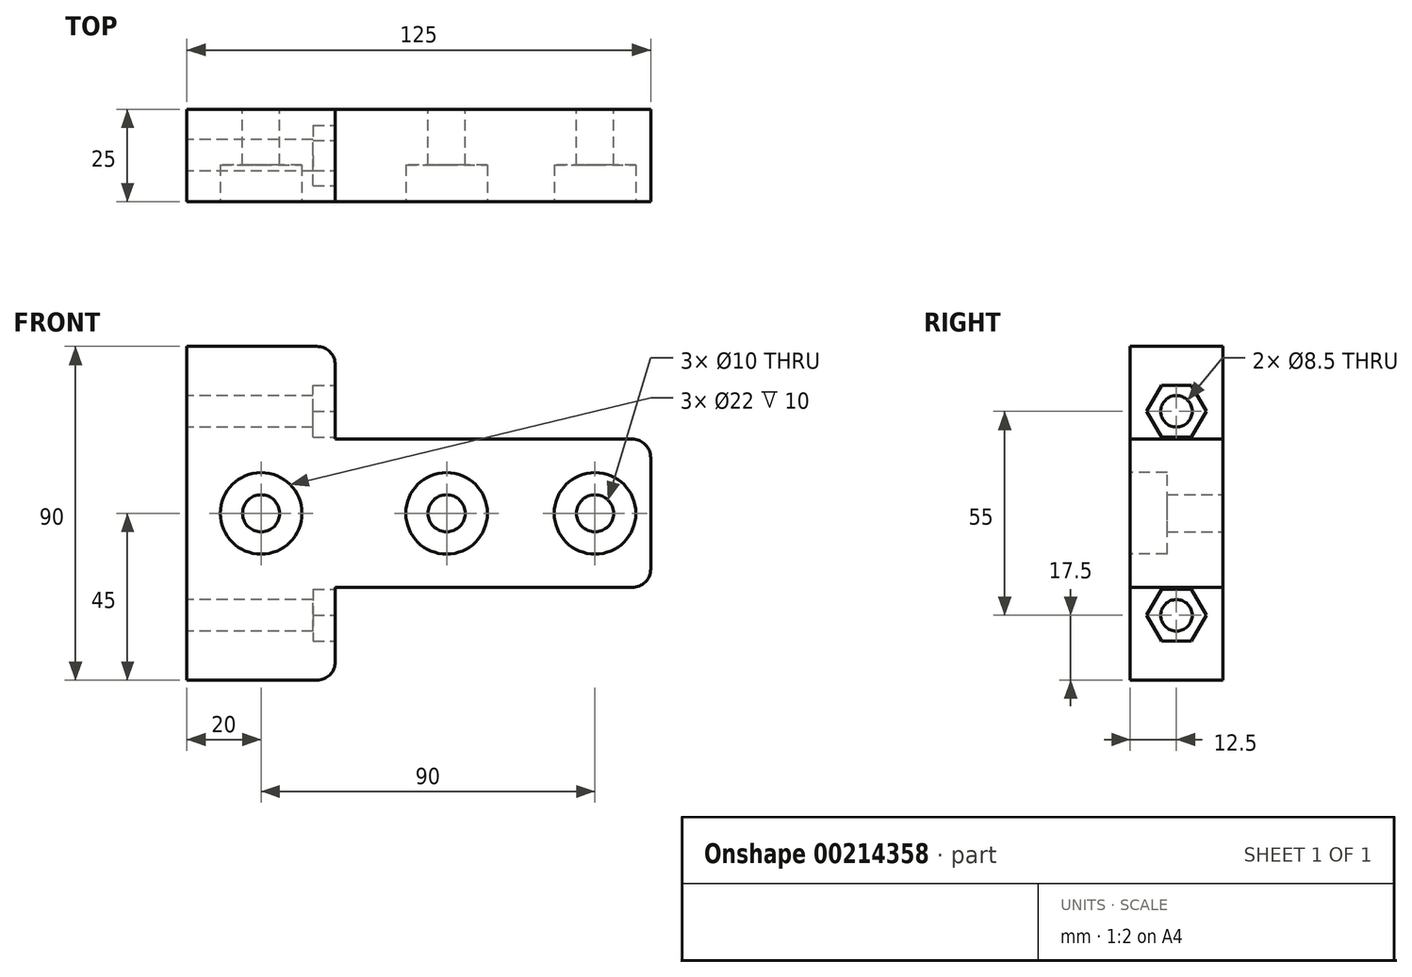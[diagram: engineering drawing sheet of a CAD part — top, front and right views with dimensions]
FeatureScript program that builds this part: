
annotation { "Feature Type Name" : "Feature", "Feature Type Description" : "" }
export const myFeature = defineFeature(function(context is Context, id is Id, definition is map)
    precondition{}
    {
        {
            var Q0;
            Q0=qCreatedBy(makeId("Front.planeOp"),FACE);
            var sketch = newSketch(context, id + "F0", { "sketchPlane" : qUnion([Q0])});
            skLineSegment(sketch, "E0.bottom", {"start": v(55, 20) * mm, "end": v(-70, 20) * mm});
            skLineSegment(sketch, "E0.top", {"start": v(55, -20) * mm, "end": v(-70, -20) * mm});
            skLineSegment(sketch, "E0.right", {"start": v(-70, 20) * mm, "end": v(-70, -20) * mm});
            skPoint(sketch, "E0.middle", {"position": v(0, 0) * mm});
            skCircle(sketch, "E1", {"center": v(0, 0) * mm, "radius": 5 * mm});
            skCircle(sketch, "E2", {"center": v(40, 0) * mm, "radius": 5 * mm});
            skCircle(sketch, "E3", {"center": v(-50, 0) * mm, "radius": 5 * mm});
            skLineSegment(sketch, "E4", {"start": v(55, 20) * mm, "end": v(55, -20) * mm});
            skSolve(sketch);
        }
        {
            var Q0;
            Q0=qSketchRegion(id+"F0",true);
            extrude(context, id + "F1", {"entities" : qUnion([Q0]), "depth" : 25 * mm});
        }
        {
            var Q0;
            Q0=makeQuery(id+"F1.opExtrude","CAP_FACE",FACE,{"disambiguationData":[OSD([sQuery(id+"F0.wireOp",EDGE,"E0.bottom"),sQuery(id+"F0.wireOp",EDGE,"E0.top"),sQuery(id+"F0.wireOp",EDGE,"E0.right"),sQuery(id+"F0.wireOp",EDGE,"E1"),sQuery(id+"F0.wireOp",EDGE,"E2"),sQuery(id+"F0.wireOp",EDGE,"E3"),sQuery(id+"F0.wireOp",EDGE,"E4")])],"isStart":false});
            var sketch = newSketch(context, id + "F2", { "sketchPlane" : qUnion([Q0])});
            skCircle(sketch, "E5", {"center": v(-50, 0) * mm, "radius": 11 * mm});
            skCircle(sketch, "E6", {"center": v(0, 0) * mm, "radius": 11 * mm});
            skCircle(sketch, "E7", {"center": v(40, 0) * mm, "radius": 11 * mm});
            skSolve(sketch);
        }
        {
            var Q0;
            Q0=qSketchRegion(id+"F2",true);
            extrude(context, id + "F3", {"entities" : qUnion([Q0]), "operationType" : NewBodyOperationType.REMOVE, "oppositeDirection" : true, "depth" : 10 * mm});
        }
        {
            var Q0;
            Q0=makeQuery(id+"F1.opExtrude","CAP_FACE",FACE,{"disambiguationData":[OSD([sQuery(id+"F0.wireOp",EDGE,"E0.bottom"),sQuery(id+"F0.wireOp",EDGE,"E0.top"),sQuery(id+"F0.wireOp",EDGE,"E0.right"),sQuery(id+"F0.wireOp",EDGE,"E1"),sQuery(id+"F0.wireOp",EDGE,"E2"),sQuery(id+"F0.wireOp",EDGE,"E3"),sQuery(id+"F0.wireOp",EDGE,"E4")])],"isStart":true});
            var sketch = newSketch(context, id + "F4", { "sketchPlane" : qUnion([Q0])});
            skLineSegment(sketch, "E8", {"start": v(30, 20) * mm, "end": v(30, 45) * mm});
            skLineSegment(sketch, "E9", {"start": v(30, 45) * mm, "end": v(70, 45) * mm});
            skLineSegment(sketch, "E10", {"start": v(70, 45) * mm, "end": v(70, 20) * mm});
            skLineSegment(sketch, "E11", {"start": v(70, 20) * mm, "end": v(30, 20) * mm});
            skLineSegment(sketch, "E12", {"start": v(70, -20) * mm, "end": v(70, -45) * mm});
            skLineSegment(sketch, "E13", {"start": v(70, -45) * mm, "end": v(30, -45) * mm});
            skLineSegment(sketch, "E14", {"start": v(30, -45) * mm, "end": v(30, -20) * mm});
            skLineSegment(sketch, "E15", {"start": v(30, -20) * mm, "end": v(70, -20) * mm});
            skSolve(sketch);
        }
        {
            var Q0;
            Q0=qSketchRegion(id+"F4",true);
            extrude(context, id + "F5", {"entities" : qUnion([Q0]), "operationType" : NewBodyOperationType.ADD, "oppositeDirection" : true, "depth" : 25 * mm});
        }
        {
            var Q0;
            Q0=makeQuery(id+"F5.boolean.opBoolean","MERGE",FACE,{"derivedFrom":[makeQuery(id+"F1.opExtrude","SWEPT_FACE",FACE,{"disambiguationData":[OSD([sQuery(id+"F0.wireOp",EDGE,"E0.right")])]}),makeQuery(id+"F5.opExtrude","SWEPT_FACE",FACE,{"disambiguationData":[OSD([sQuery(id+"F4.wireOp",EDGE,"E10")])]}),makeQuery(id+"F5.opExtrude","SWEPT_FACE",FACE,{"disambiguationData":[OSD([sQuery(id+"F4.wireOp",EDGE,"E12")])]})]});
            var sketch = newSketch(context, id + "F6", { "sketchPlane" : qUnion([Q0])});
            skCircle(sketch, "E16", {"center": v(12.5, 27.5) * mm, "radius": 4.25 * mm});
            skCircle(sketch, "E17", {"center": v(12.5, -27.5) * mm, "radius": 4.25 * mm});
            skSolve(sketch);
        }
        {
            var Q0;
            Q0=qSketchRegion(id+"F6",true);
            extrude(context, id + "F7", {"entities" : qUnion([Q0]), "operationType" : NewBodyOperationType.REMOVE, "endBound" : BoundingType.UP_TO_NEXT, "oppositeDirection" : true, "depth" : 25 * mm});
        }
        {
            var Q0;
            Q0=makeQuery(id+"F5.opExtrude","SWEPT_FACE",FACE,{"disambiguationData":[OSD([sQuery(id+"F4.wireOp",EDGE,"E8")])]});
            var sketch = newSketch(context, id + "F8", { "sketchPlane" : qUnion([Q0])});
            skCircle(sketch, "E18.cCircle", {"center": v(-12.5, 27.5) * mm, "radius": 7 * mm, "construction": true});
            skLineSegment(sketch, "E18.0", {"start": v(-16.54, 34.5) * mm, "end": v(-8.46, 34.5) * mm});
            skLineSegment(sketch, "E18.1", {"start": v(-8.46, 34.5) * mm, "end": v(-4.42, 27.5) * mm});
            skLineSegment(sketch, "E18.2", {"start": v(-4.42, 27.5) * mm, "end": v(-8.46, 20.5) * mm});
            skLineSegment(sketch, "E18.3", {"start": v(-8.46, 20.5) * mm, "end": v(-16.54, 20.5) * mm});
            skLineSegment(sketch, "E18.4", {"start": v(-16.54, 20.5) * mm, "end": v(-20.58, 27.5) * mm});
            skLineSegment(sketch, "E18.5", {"start": v(-20.58, 27.5) * mm, "end": v(-16.54, 34.5) * mm});
            skPoint(sketch, "E18.0.midPoint", {"position": v(-12.5, 34.5) * mm});
            skLineSegment(sketch, "E19.MirrorCS", {"start": v(-16.54, -20.5) * mm, "end": v(-20.58, -27.5) * mm});
            skLineSegment(sketch, "E20.MirrorCS", {"start": v(-8.46, -20.5) * mm, "end": v(-16.54, -20.5) * mm});
            skLineSegment(sketch, "E21.MirrorCS", {"start": v(-4.42, -27.5) * mm, "end": v(-8.46, -20.5) * mm});
            skLineSegment(sketch, "E22.MirrorCS", {"start": v(-8.46, -34.5) * mm, "end": v(-4.42, -27.5) * mm});
            skLineSegment(sketch, "E23.MirrorCS", {"start": v(-20.58, -27.5) * mm, "end": v(-16.54, -34.5) * mm});
            skLineSegment(sketch, "E24.MirrorCS", {"start": v(-16.54, -34.5) * mm, "end": v(-8.46, -34.5) * mm});
            skSolve(sketch);
        }
        {
            var Q0;
            Q0=qSketchRegion(id+"F8",true);
            extrude(context, id + "F9", {"entities" : qUnion([Q0]), "operationType" : NewBodyOperationType.REMOVE, "oppositeDirection" : true, "depth" : 6 * mm});
        }
        {
            var Q0;
            Q0=makeQuery(id+"F5.opExtrude","SWEPT_EDGE",EDGE,{"disambiguationData":[OSD([sQuery(id+"F0.wireOp",EDGE,"E0.bottom"),sQuery(id+"F4.wireOp",EDGE,"E8"),sQuery(id+"F4.wireOp",EDGE,"E11")])]});
            var Q1;
            Q1=makeQuery(id+"F5.opExtrude","SWEPT_EDGE",EDGE,{"disambiguationData":[OSD([sQuery(id+"F4.wireOp",EDGE,"E8"),sQuery(id+"F4.wireOp",EDGE,"E9")])]});
            var Q2;
            Q2=makeQuery(id+"F5.opExtrude","SWEPT_EDGE",EDGE,{"disambiguationData":[OSD([sQuery(id+"F0.wireOp",EDGE,"E0.top"),sQuery(id+"F4.wireOp",EDGE,"E14"),sQuery(id+"F4.wireOp",EDGE,"E15")])]});
            var Q3;
            Q3=makeQuery(id+"F5.opExtrude","SWEPT_EDGE",EDGE,{"disambiguationData":[OSD([sQuery(id+"F4.wireOp",EDGE,"E13"),sQuery(id+"F4.wireOp",EDGE,"E14")])]});
            var Q4;
            Q4=makeQuery(id+"F1.opExtrude","SWEPT_EDGE",EDGE,{"disambiguationData":[OSD([sQuery(id+"F0.wireOp",EDGE,"E0.top"),sQuery(id+"F0.wireOp",EDGE,"E4")])]});
            var Q5;
            Q5=makeQuery(id+"F1.opExtrude","SWEPT_EDGE",EDGE,{"disambiguationData":[OSD([sQuery(id+"F0.wireOp",EDGE,"E0.bottom"),sQuery(id+"F0.wireOp",EDGE,"E4")])]});
            fillet(context, id + "F10", {"entities" : qUnion([Q0, Q1, Q2, Q3, Q4, Q5]), "radius" : 5 * mm, "tangentPropagation" : true, "allowEdgeOverflow" : false});
        }
    });
